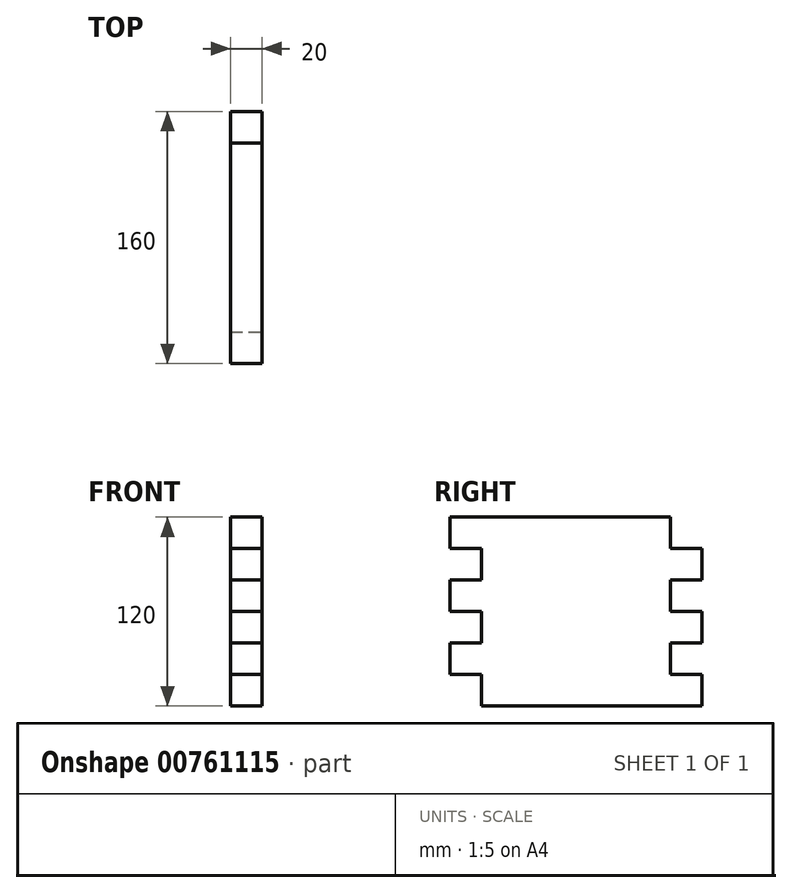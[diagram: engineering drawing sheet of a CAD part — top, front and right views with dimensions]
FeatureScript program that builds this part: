
annotation { "Feature Type Name" : "Feature", "Feature Type Description" : "" }
export const myFeature = defineFeature(function(context is Context, id is Id, definition is map)
    precondition{}
    {
        {
            var Q0;
            Q0=qCreatedBy(makeId("Right.planeOp"),FACE);
            var sketch = newSketch(context, id + "F0", { "sketchPlane" : qUnion([Q0])});
            skLineSegment(sketch, "E0.bottom", {"start": v(-244.9, 140.94) * mm, "end": v(-84.9, 140.94) * mm});
            skLineSegment(sketch, "E0.top", {"start": v(-244.9, 20.94) * mm, "end": v(-84.9, 20.94) * mm});
            skLineSegment(sketch, "E0.left", {"start": v(-244.9, 140.94) * mm, "end": v(-244.9, 20.94) * mm});
            skLineSegment(sketch, "E0.right", {"start": v(-84.9, 140.94) * mm, "end": v(-84.9, 20.94) * mm});
            skSolve(sketch);
        }
        {
            var Q0;
            Q0=qSketchRegion(id+"F0",true);
            extrude(context, id + "F1", {"entities" : qUnion([Q0]), "depth" : 20 * mm, "offsetDistance" : 25 * mm});
        }
        {
            var Q0;
            Q0=makeQuery(id+"F1.opExtrude","CAP_FACE",FACE,{"disambiguationData":[OSD([sQuery(id+"F0.wireOp",EDGE,"E0.bottom"),sQuery(id+"F0.wireOp",EDGE,"E0.top"),sQuery(id+"F0.wireOp",EDGE,"E0.left"),sQuery(id+"F0.wireOp",EDGE,"E0.right")])],"isStart":false});
            var sketch = newSketch(context, id + "F2", { "sketchPlane" : qUnion([Q0])});
            skLineSegment(sketch, "E1.bottom", {"start": v(-244.9, 120.94) * mm, "end": v(-224.9, 120.94) * mm});
            skLineSegment(sketch, "E1.top", {"start": v(-244.9, 100.94) * mm, "end": v(-224.9, 100.94) * mm});
            skLineSegment(sketch, "E1.left", {"start": v(-244.9, 120.94) * mm, "end": v(-244.9, 100.94) * mm});
            skLineSegment(sketch, "E1.right", {"start": v(-224.9, 120.94) * mm, "end": v(-224.9, 100.94) * mm});
            skSolve(sketch);
        }
        {
            var Q0;
            Q0=qSketchRegion(id+"F2",true);
            extrude(context, id + "F3", {"entities" : qUnion([Q0]), "operationType" : NewBodyOperationType.REMOVE, "oppositeDirection" : true, "depth" : 20 * mm, "offsetDistance" : 25 * mm});
        }
        {
            var Q0;
            Q0=makeQuery(id+"F1.opExtrude","CAP_FACE",FACE,{"disambiguationData":[OSD([sQuery(id+"F0.wireOp",EDGE,"E0.bottom"),sQuery(id+"F0.wireOp",EDGE,"E0.top"),sQuery(id+"F0.wireOp",EDGE,"E0.left"),sQuery(id+"F0.wireOp",EDGE,"E0.right")])],"isStart":false});
            var sketch = newSketch(context, id + "F4", { "sketchPlane" : qUnion([Q0])});
            skLineSegment(sketch, "E2.bottom", {"start": v(-244.9, 80.94) * mm, "end": v(-224.9, 80.94) * mm});
            skLineSegment(sketch, "E2.top", {"start": v(-244.9, 60.94) * mm, "end": v(-224.9, 60.94) * mm});
            skLineSegment(sketch, "E2.left", {"start": v(-244.9, 80.94) * mm, "end": v(-244.9, 60.94) * mm});
            skLineSegment(sketch, "E2.right", {"start": v(-224.9, 80.94) * mm, "end": v(-224.9, 60.94) * mm});
            skSolve(sketch);
        }
        {
            var Q0;
            Q0=qSketchRegion(id+"F4",true);
            extrude(context, id + "F5", {"entities" : qUnion([Q0]), "operationType" : NewBodyOperationType.REMOVE, "oppositeDirection" : true, "depth" : 20 * mm, "offsetDistance" : 25 * mm});
        }
        {
            var Q0;
            Q0=makeQuery(id+"F1.opExtrude","CAP_FACE",FACE,{"disambiguationData":[OSD([sQuery(id+"F0.wireOp",EDGE,"E0.bottom"),sQuery(id+"F0.wireOp",EDGE,"E0.top"),sQuery(id+"F0.wireOp",EDGE,"E0.left"),sQuery(id+"F0.wireOp",EDGE,"E0.right")])],"isStart":false});
            var sketch = newSketch(context, id + "F6", { "sketchPlane" : qUnion([Q0])});
            skLineSegment(sketch, "E3.bottom", {"start": v(-244.9, 20.94) * mm, "end": v(-224.9, 20.94) * mm});
            skLineSegment(sketch, "E3.top", {"start": v(-244.9, 40.94) * mm, "end": v(-224.9, 40.94) * mm});
            skLineSegment(sketch, "E3.left", {"start": v(-244.9, 20.94) * mm, "end": v(-244.9, 40.94) * mm});
            skLineSegment(sketch, "E3.right", {"start": v(-224.9, 20.94) * mm, "end": v(-224.9, 40.94) * mm});
            skSolve(sketch);
        }
        {
            var Q0;
            Q0=qSketchRegion(id+"F6",true);
            extrude(context, id + "F7", {"entities" : qUnion([Q0]), "operationType" : NewBodyOperationType.REMOVE, "oppositeDirection" : true, "depth" : 20 * mm, "offsetDistance" : 25 * mm});
        }
        {
            var Q0;
            Q0=makeQuery(id+"F1.opExtrude","CAP_FACE",FACE,{"disambiguationData":[OSD([sQuery(id+"F0.wireOp",EDGE,"E0.bottom"),sQuery(id+"F0.wireOp",EDGE,"E0.top"),sQuery(id+"F0.wireOp",EDGE,"E0.left"),sQuery(id+"F0.wireOp",EDGE,"E0.right")])],"isStart":false});
            var sketch = newSketch(context, id + "F8", { "sketchPlane" : qUnion([Q0])});
            skLineSegment(sketch, "E4.bottom", {"start": v(-84.9, 140.94) * mm, "end": v(-104.9, 140.94) * mm});
            skLineSegment(sketch, "E4.top", {"start": v(-84.9, 120.94) * mm, "end": v(-104.9, 120.94) * mm});
            skLineSegment(sketch, "E4.left", {"start": v(-84.9, 140.94) * mm, "end": v(-84.9, 120.94) * mm});
            skLineSegment(sketch, "E4.right", {"start": v(-104.9, 140.94) * mm, "end": v(-104.9, 120.94) * mm});
            skSolve(sketch);
        }
        {
            var Q0;
            Q0=qSketchRegion(id+"F8",true);
            extrude(context, id + "F9", {"entities" : qUnion([Q0]), "operationType" : NewBodyOperationType.REMOVE, "oppositeDirection" : true, "depth" : 20 * mm, "offsetDistance" : 25 * mm});
        }
        {
            var Q0;
            Q0=makeQuery(id+"F1.opExtrude","CAP_FACE",FACE,{"disambiguationData":[OSD([sQuery(id+"F0.wireOp",EDGE,"E0.bottom"),sQuery(id+"F0.wireOp",EDGE,"E0.top"),sQuery(id+"F0.wireOp",EDGE,"E0.left"),sQuery(id+"F0.wireOp",EDGE,"E0.right")])],"isStart":false});
            var sketch = newSketch(context, id + "F10", { "sketchPlane" : qUnion([Q0])});
            skLineSegment(sketch, "E5.bottom", {"start": v(-84.9, 100.94) * mm, "end": v(-104.9, 100.94) * mm});
            skLineSegment(sketch, "E5.top", {"start": v(-84.9, 80.94) * mm, "end": v(-104.9, 80.94) * mm});
            skLineSegment(sketch, "E5.left", {"start": v(-84.9, 100.94) * mm, "end": v(-84.9, 80.94) * mm});
            skLineSegment(sketch, "E5.right", {"start": v(-104.9, 100.94) * mm, "end": v(-104.9, 80.94) * mm});
            skSolve(sketch);
        }
        {
            var Q0;
            Q0=qSketchRegion(id+"F10",true);
            extrude(context, id + "F11", {"entities" : qUnion([Q0]), "operationType" : NewBodyOperationType.REMOVE, "oppositeDirection" : true, "depth" : 20 * mm, "offsetDistance" : 25 * mm});
        }
        {
            var Q0;
            Q0=makeQuery(id+"F1.opExtrude","CAP_FACE",FACE,{"disambiguationData":[OSD([sQuery(id+"F0.wireOp",EDGE,"E0.bottom"),sQuery(id+"F0.wireOp",EDGE,"E0.top"),sQuery(id+"F0.wireOp",EDGE,"E0.left"),sQuery(id+"F0.wireOp",EDGE,"E0.right")])],"isStart":false});
            var sketch = newSketch(context, id + "F12", { "sketchPlane" : qUnion([Q0])});
            skLineSegment(sketch, "E6.bottom", {"start": v(-84.9, 60.94) * mm, "end": v(-104.9, 60.94) * mm});
            skLineSegment(sketch, "E6.top", {"start": v(-84.9, 40.94) * mm, "end": v(-104.9, 40.94) * mm});
            skLineSegment(sketch, "E6.left", {"start": v(-84.9, 60.94) * mm, "end": v(-84.9, 40.94) * mm});
            skLineSegment(sketch, "E6.right", {"start": v(-104.9, 60.94) * mm, "end": v(-104.9, 40.94) * mm});
            skSolve(sketch);
        }
        {
            var Q0;
            Q0=qSketchRegion(id+"F12",true);
            extrude(context, id + "F13", {"entities" : qUnion([Q0]), "operationType" : NewBodyOperationType.REMOVE, "oppositeDirection" : true, "depth" : 20 * mm, "offsetDistance" : 25 * mm});
        }
    });
